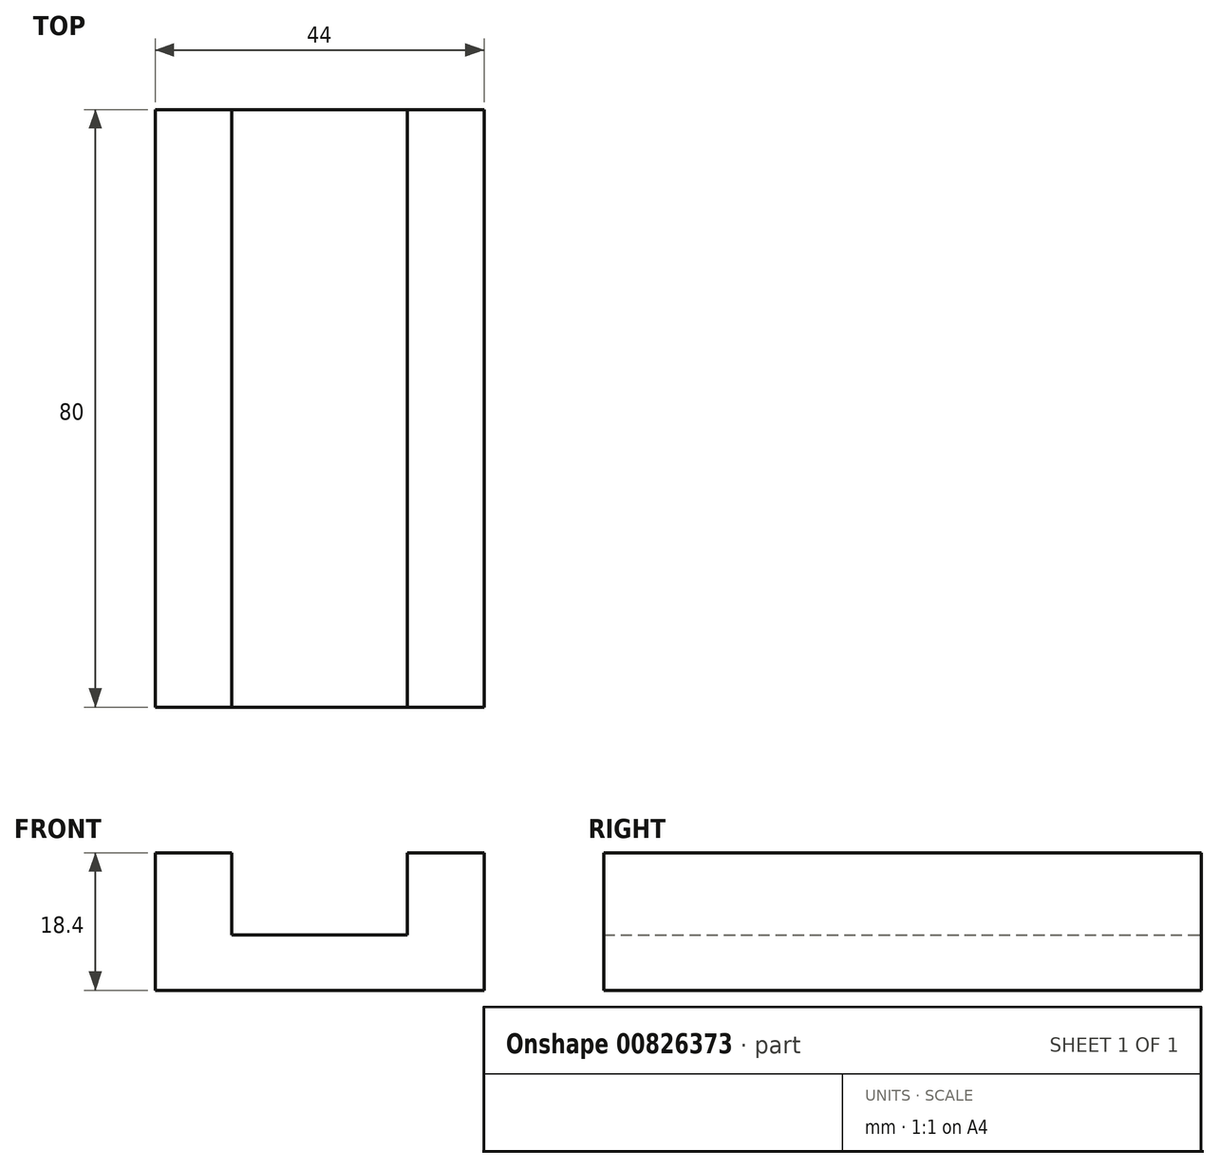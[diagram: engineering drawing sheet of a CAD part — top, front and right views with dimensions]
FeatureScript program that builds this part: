
annotation { "Feature Type Name" : "Feature", "Feature Type Description" : "" }
export const myFeature = defineFeature(function(context is Context, id is Id, definition is map)
    precondition{}
    {
        {
            var Q0;
            Q0=qCreatedBy(makeId("Front.planeOp"),FACE);
            var sketch = newSketch(context, id + "F0", { "sketchPlane" : qUnion([Q0])});
            skLineSegment(sketch, "E0.bottom", {"start": v(-22, -9.2) * mm, "end": v(22, -9.2) * mm});
            skLineSegment(sketch, "E0.top", {"start": v(-22, 9.2) * mm, "end": v(22, 9.2) * mm});
            skLineSegment(sketch, "E0.left", {"start": v(-22, -9.2) * mm, "end": v(-22, 9.2) * mm});
            skLineSegment(sketch, "E0.right", {"start": v(22, -9.2) * mm, "end": v(22, 9.2) * mm});
            skPoint(sketch, "E0.middle", {"position": v(0, 0) * mm});
            skLineSegment(sketch, "E1.bottom", {"start": v(-11.75, -1.8) * mm, "end": v(11.75, -1.8) * mm});
            skLineSegment(sketch, "E1.top", {"start": v(-11.75, 9.2) * mm, "end": v(11.75, 9.2) * mm});
            skLineSegment(sketch, "E1.left", {"start": v(-11.75, -1.8) * mm, "end": v(-11.75, 9.2) * mm});
            skLineSegment(sketch, "E1.right", {"start": v(11.75, -1.8) * mm, "end": v(11.75, 9.2) * mm});
            skPoint(sketch, "E1.middle", {"position": v(0, 3.7) * mm});
            skSolve(sketch);
        }
        {
            var Q0;
            Q0=makeQuery(id+"F0.imprint","IMPRINT",FACE,{"disambiguationData":[TD([[makeQuery(id+"F0.imprint","IMPRINT",EDGE,{"derivedFrom":sQuery(id+"F0.wireOp",EDGE,"E0.bottom")}),1.0]])]});
            extrude(context, id + "F1", {"entities" : qUnion([Q0]), "depth" : 80 * mm, "offsetDistance" : 25 * mm});
        }
    });
